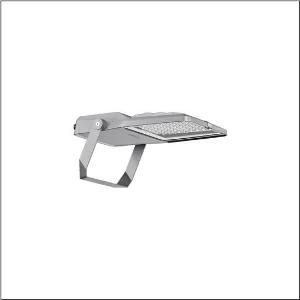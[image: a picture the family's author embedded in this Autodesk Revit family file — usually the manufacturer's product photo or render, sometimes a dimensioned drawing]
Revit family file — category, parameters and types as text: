
# Revit family: floodlight_fl_21_iq_mini___pl43_5xa7772b2a1a_654d
name_source: partatom
category: Lighting Fixtures
units: mm (PartAtom-declared; Revit-internal decimal feet)

## family parameters
Cut with Voids When Loaded = No
Host = Face
Light Source = No
Part Type = Normal
Room Calculation Point = No
Round Connector Dimension = Use Diameter
Shared = No

## types (1)
- --- (1 x LED, 6400 lm, 45.5 W, 3000K)
    Apparent Load = 46 VA
    CIE Flux Codes = 27 78 99 100 100
    Color Rendering = 70
    Color Temperature = 3000K
    Default Elevation = 1800 mm
    Description = Floodlight FL 21 iQ mini, floodlight, primary light control with lens, of PMMA, primary optical cover: protective disc, of toughened safety glass, transparent, light distribution: PL43, light emission: direct distribution, installation type: surface-mounted, LED, High Power LED, rated luminous flux: 6.400lm, luminous efficacy: 141lm/W, light colour: 730, colour temperature: 3000K, control: Street-Remote, Auto-Match, Temp-Guard, Night-Set, Smart-Wire, Desk-Remote (wireless, voltage-free reading and setting of iQ features in the workshop via application-optimized NFC function/RFID function), optimised constant luminous flux control (CLO 2.0), with terminal, 6-pole, mains connection: 220..240V, AC, 50/60Hz, start of lifetime: 46W, end of service life: 48W, reduction: 22W, luminaire housing, of diecast aluminium, powder-coated, Siteco® metallic grey (DB 702S), corrosivity category C5 mid according to DIN EN ISO 12944, sealing non-destructively replaceable, mounting bracket, of steel, galvanised, powder-coated, Siteco® metallic grey (DB 702S), protection rating (complete): IP66, insulation class (complete): insulation class II (safety insulation), certification: CE, ENEC, VDE, protection symbol: D, impact resistance: IK08, permissible operating ambient temperature: -40..+40°C, permissible operating ambient temperature for outdoor applications: -40..+50°C, standard: DIN EN 12944, LABS conformity tested according to VDMA 24364:2018-05, packaging unit: 1 piece

Light Distribution: PL43
    Height = 70 mm
    Lamp = 1 x LED
    Lamp Light Flux = 6400 lm
    Lamp Power = 45.5 W
    Lamp count = 1
    Length = 485 mm
    Luminous efficacy = 141 lm/W
    Manufacturer = Siteco
    ModVariant = No
    Model = 5XA7772B2A1A
    Number of Poles = 1
    OnlyDefault = Yes
    Power Factor = 1
    Product Name = Floodlight FL 21 iQ mini | PL43
    Product group = floodlight | pylon annexe
    ProductGroupID = 6200
    Protection Class = Protection class II
    Protection Degree = IP 66
    RLX_Detail_Level = 1
    RLX_Emergency_Light_Flux = 0 lm
    RLX_Emergency_Type = 0
    RLX_Emergency_Type_DB = No
    RlxData = <blob elided: 95937 chars, md5=410c065c>
    Socket = socket
    Standby Power = 0 W
    System Light Flux = 6400 lm
    System Power = 46 W
    Type Comments = factory setting: luminous flux: 100 % | dim-lin: 254 | 463 mA
    Type Image = l_1006845.jpg
    URL = http://relux.com
    VarID = @adj_095269
    Voltage = 0 V
    Weight = 0.00 kg
    Width = 337 mm

## geometry (parser evidence)
native form markers: Blend x4, Sweep x14
no freeform markers — native parametric forms only
